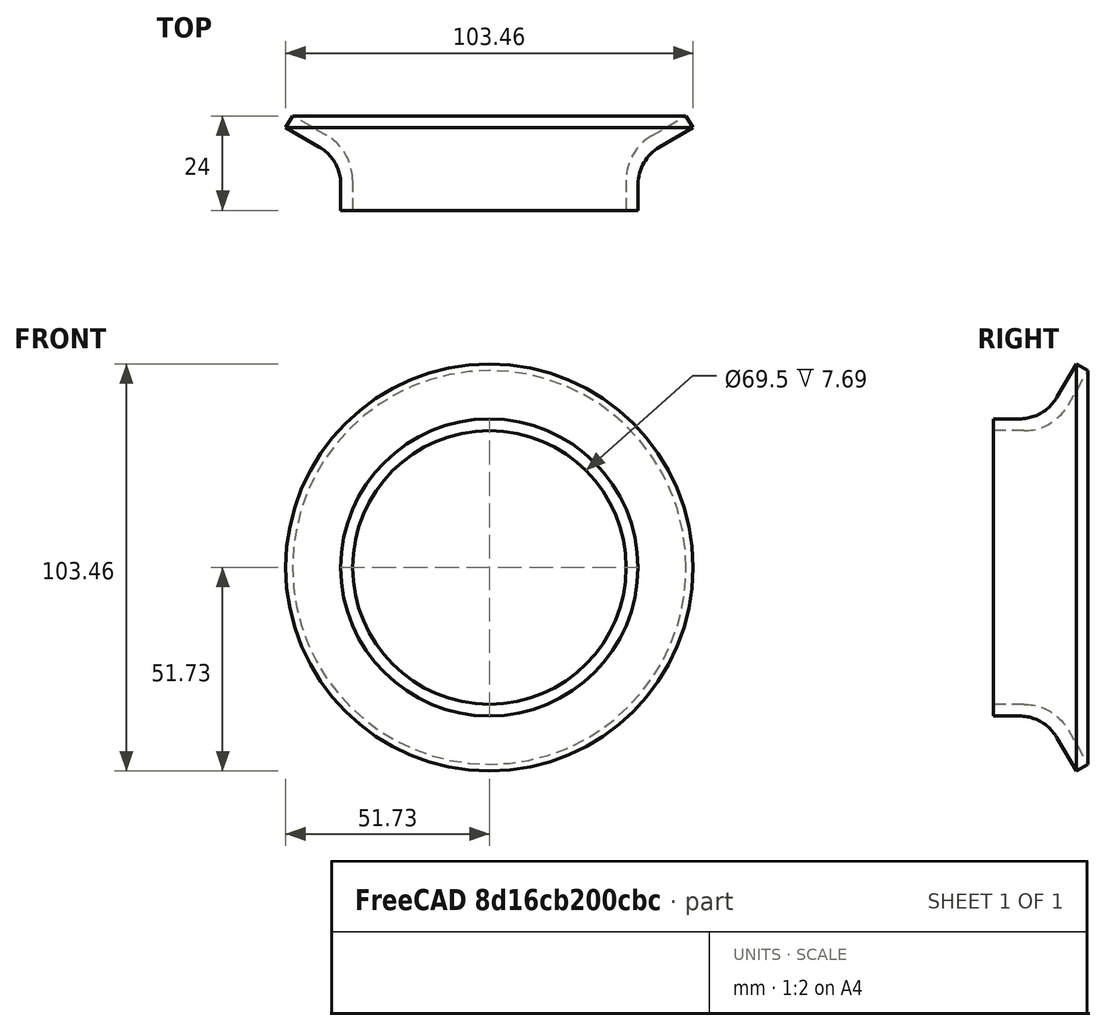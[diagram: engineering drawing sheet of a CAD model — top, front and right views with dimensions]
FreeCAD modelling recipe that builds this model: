
FCSTD DOCUMENT  (FreeCAD 0.19R24291 (Git))
Label: adapt_lens_hood1
License: All rights reserved
LicenseURL: http://en.wikipedia.org/wiki/All_rights_reserved
objects: Sketcher::SketchObject×1, PartDesign::Revolution×1, PartDesign::Body×1
note: 4 computed .brp shape members not serialized (recipe doc carries the construction recipe); baked Part::Feature solids carry a one-line shape summary decoded from their .brp

FEATURE [Sketcher::SketchObject] Sketch
  FullyConstrained = true
  MapMode = 5
  Support = -> [XY_Plane]
  sketch-geometry (8):
    g0: LineSegment StartX=43.25 StartY=12.1029 StartZ=0 EndX=51.7321 EndY=17 EndZ=0
    g1: LineSegment StartX=41.25 StartY=14.9482 StartZ=0 EndX=50 EndY=20 EndZ=0
    g2: LineSegment StartX=51.7321 StartY=17 StartZ=0 EndX=50 EndY=20 EndZ=0
    g3: LineSegment StartX=34.75 StartY=3.68985 StartZ=0 EndX=34.75 EndY=-4 EndZ=0
    g4: LineSegment StartX=37.75 StartY=2.57661 StartZ=0 EndX=37.75 EndY=-4 EndZ=0
    g5: LineSegment StartX=34.75 StartY=-4 StartZ=0 EndX=37.75 EndY=-4 EndZ=0
    g6: ArcOfCircle CenterX=48.75 CenterY=2.57661 CenterZ=0 NormalX=0 NormalY=0 NormalZ=1 AngleXU=0 Radius=11 StartAngle=2.0944 EndAngle=3.14159
    g7: ArcOfCircle CenterX=47.75 CenterY=3.68985 CenterZ=0 NormalX=0 NormalY=0 NormalZ=1 AngleXU=0 Radius=13 StartAngle=2.0944 EndAngle=3.14159
  constraints (22):
    c: Angle(g1,g-2) = 1.0472
    c: Horizontal(g5)
    c: Perpendicular(g5,g3)
    c: DistanceX(g3,g4) = 3
    c: Parallel(g4,g3)
    c: Coincident(g4,g5)
    c: Parallel(g0,g1)
    c: Coincident(g0,g2)
    c: Perpendicular(g2,g1)
    c: Coincident(g1,g2)
    c: Tangent(g0,g6) = 1.5708
    c: Tangent(g4,g6) = -1.5708
    c: Tangent(g1,g7) = 1.5708
    c: Tangent(g3,g7) = -1.5708
    c: DistanceY(g3,g-1) = 4
    c: Coincident(g5,g3)
    c: DistanceX(g-1,g1) = 50
    c: DistanceY(g-1,g1) = 20
    c: DistanceX(g-1,g3) = 34.75
    c: DistanceY(g-1,g0) = 17
    c: Radius(g7) = 13
    c: Radius(g6) = 11
FEATURE [PartDesign::Revolution] Revolution
  Angle = 360
  Axis = (0,1,0)
  Base = (0,0,0)
  Profile = -> Sketch
  ReferenceAxis = -> Sketch [V_Axis]
  Reversed = true
FEATURE [PartDesign::Body] Body
  Group = -> [Sketch,Revolution]
  Origin = -> Origin
  Tip = -> Revolution
